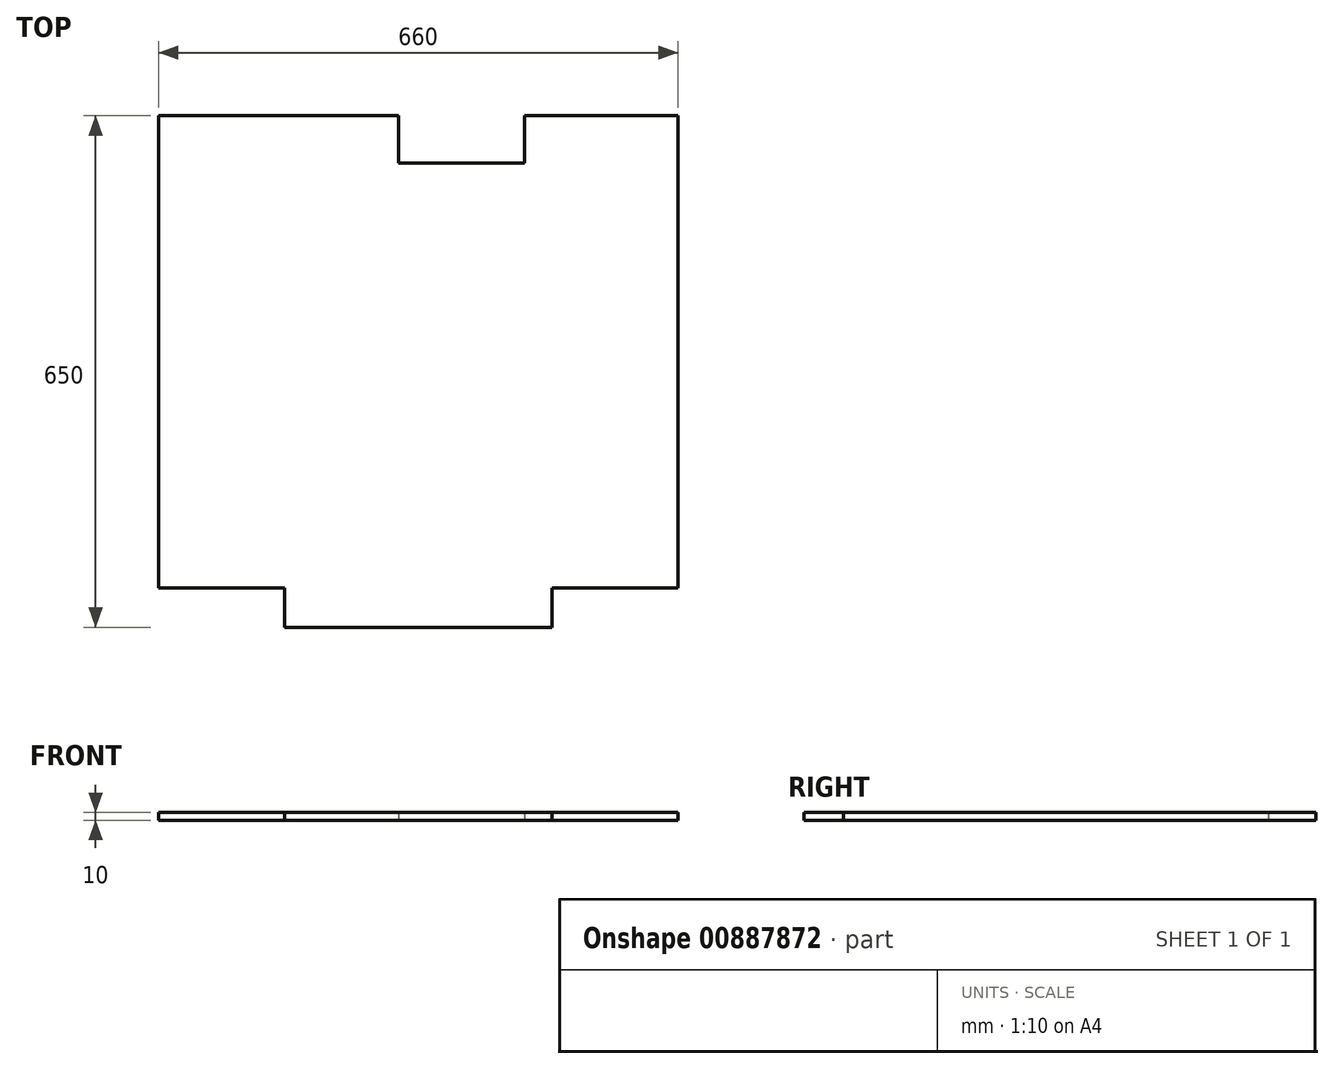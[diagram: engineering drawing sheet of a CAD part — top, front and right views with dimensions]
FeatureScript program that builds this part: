
annotation { "Feature Type Name" : "Feature", "Feature Type Description" : "" }
export const myFeature = defineFeature(function(context is Context, id is Id, definition is map)
    precondition{}
    {
        {
            var Q0;
            Q0=qCreatedBy(makeId("Top.planeOp"),FACE);
            var sketch = newSketch(context, id + "F0", { "sketchPlane" : qUnion([Q0])});
            skLineSegment(sketch, "E0.bottom", {"start": v(-330, 325) * mm, "end": v(330, 325) * mm});
            skLineSegment(sketch, "E0.top", {"start": v(-330, -325) * mm, "end": v(330, -325) * mm});
            skLineSegment(sketch, "E0.left", {"start": v(-330, 325) * mm, "end": v(-330, -325) * mm});
            skLineSegment(sketch, "E0.right", {"start": v(330, 325) * mm, "end": v(330, -325) * mm});
            skPoint(sketch, "E0.middle", {"position": v(0, 0) * mm});
            skLineSegment(sketch, "E1.bottom", {"start": v(-24.95, 325) * mm, "end": v(135.05, 325) * mm});
            skLineSegment(sketch, "E1.top", {"start": v(-24.95, 265) * mm, "end": v(135.05, 265) * mm});
            skLineSegment(sketch, "E1.left", {"start": v(-24.95, 325) * mm, "end": v(-24.95, 265) * mm});
            skLineSegment(sketch, "E1.right", {"start": v(135.05, 325) * mm, "end": v(135.05, 265) * mm});
            skLineSegment(sketch, "E2.bottom", {"start": v(330, -325) * mm, "end": v(170, -325) * mm});
            skLineSegment(sketch, "E2.top", {"start": v(330, -275) * mm, "end": v(170, -275) * mm});
            skLineSegment(sketch, "E2.left", {"start": v(330, -325) * mm, "end": v(330, -275) * mm});
            skLineSegment(sketch, "E2.right", {"start": v(170, -325) * mm, "end": v(170, -275) * mm});
            skLineSegment(sketch, "E3.MirrorCS", {"start": v(-330, -275) * mm, "end": v(-170, -275) * mm});
            skLineSegment(sketch, "E4.MirrorCS", {"start": v(-170, -325) * mm, "end": v(-170, -275) * mm});
            skSolve(sketch);
        }
        {
            var Q0;
            Q0=makeQuery(id+"F0.imprint","IMPRINT",FACE,{"disambiguationData":[TD([[makeQuery(id+"F0.imprint","IMPRINT",EDGE,{"derivedFrom":sQuery(id+"F0.wireOp",EDGE,"E0.bottom")}),-1.0]])]});
            extrude(context, id + "F1", {"entities" : qUnion([Q0]), "depth" : 10 * mm, "offsetDistance" : 25 * mm});
        }
    });
